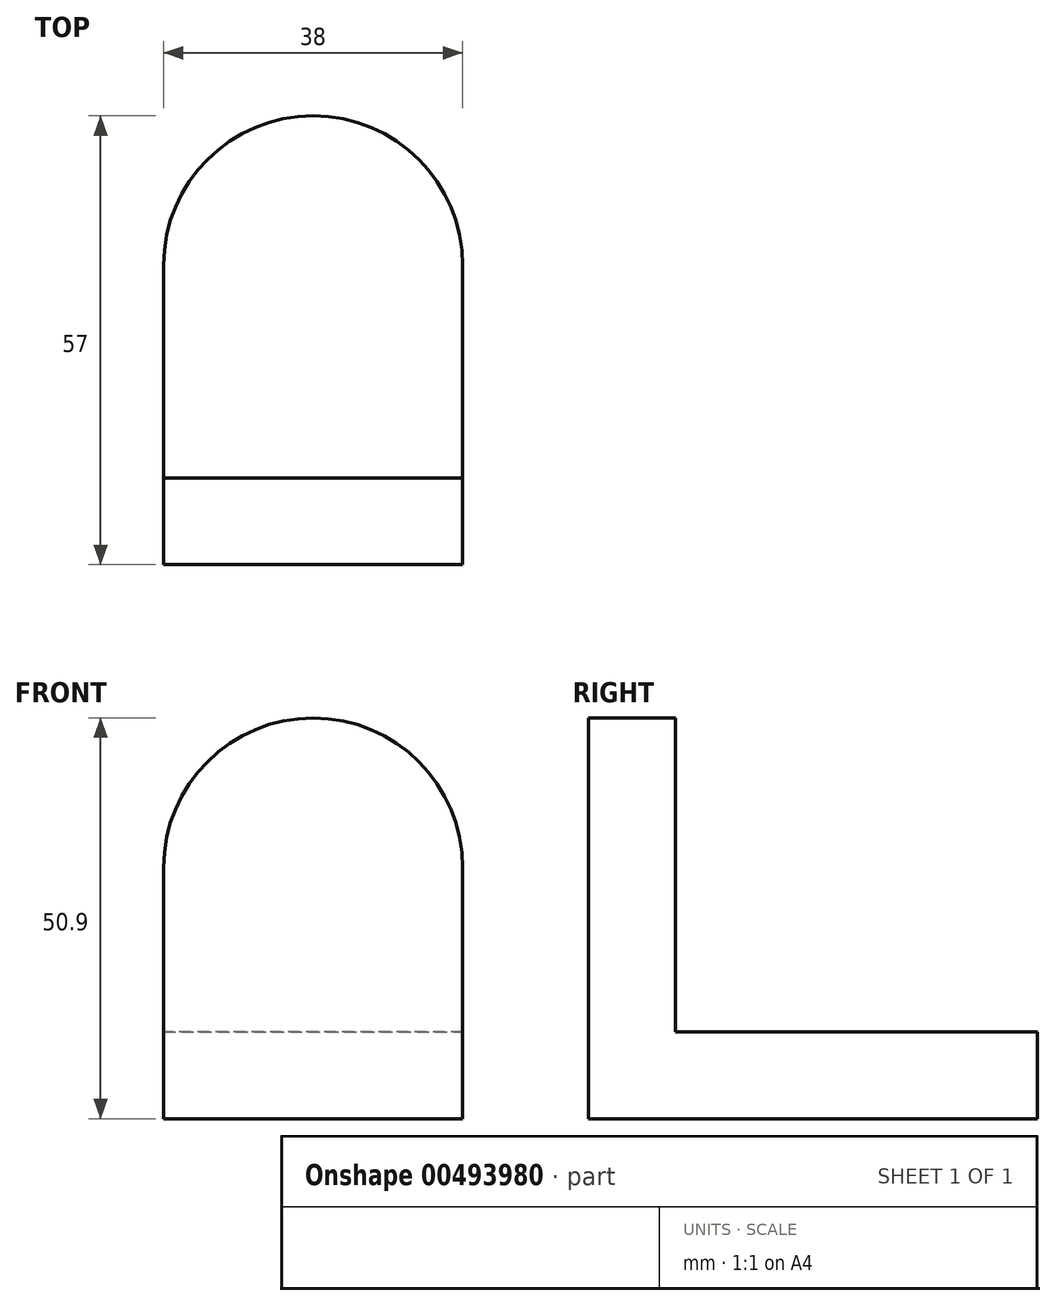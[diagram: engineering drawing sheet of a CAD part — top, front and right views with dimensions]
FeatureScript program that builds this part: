
annotation { "Feature Type Name" : "Feature", "Feature Type Description" : "" }
export const myFeature = defineFeature(function(context is Context, id is Id, definition is map)
    precondition{}
    {
        {
            var Q0;
            Q0=qCreatedBy(makeId("Right.planeOp"),FACE);
            var sketch = newSketch(context, id + "F0", { "sketchPlane" : qUnion([Q0])});
            skLineSegment(sketch, "E0", {"start": v(-17.26, 31.97) * mm, "end": v(-17.26, -18.93) * mm});
            skLineSegment(sketch, "E1", {"start": v(-17.26, -18.93) * mm, "end": v(39.74, -18.93) * mm});
            skLineSegment(sketch, "E2", {"start": v(39.74, -18.93) * mm, "end": v(39.74, -7.93) * mm});
            skLineSegment(sketch, "E3", {"start": v(39.74, -7.93) * mm, "end": v(-6.26, -7.93) * mm});
            skLineSegment(sketch, "E4", {"start": v(-6.26, -7.93) * mm, "end": v(-6.26, 31.97) * mm});
            skLineSegment(sketch, "E5", {"start": v(-6.26, 31.97) * mm, "end": v(-17.26, 31.97) * mm});
            skSolve(sketch);
        }
        {
            var Q0;
            Q0=makeQuery(id+"F0.imprint","IMPRINT",FACE,{"disambiguationData":[TD([[makeQuery(id+"F0.imprint","IMPRINT",EDGE,{"derivedFrom":sQuery(id+"F0.wireOp",EDGE,"E0")}),1.0]])]});
            extrude(context, id + "F1", {"entities" : qUnion([Q0]), "depth" : 38 * mm});
        }
        {
            var Q0;
            Q0=makeQuery(id+"F1.opExtrude","CAP_EDGE",EDGE,{"disambiguationData":[OSD([sQuery(id+"F0.wireOp",EDGE,"E5")])],"isStart":false});
            var Q1;
            Q1=makeQuery(id+"F1.opExtrude","CAP_EDGE",EDGE,{"disambiguationData":[OSD([sQuery(id+"F0.wireOp",EDGE,"E5")])],"isStart":true});
            fillet(context, id + "F2", {"entities" : qUnion([Q0, Q1]), "radius" : 19 * mm, "tangentPropagation" : true, "allowEdgeOverflow" : false});
        }
        {
            var Q0;
            Q0=makeQuery(id+"F1.opExtrude","CAP_EDGE",EDGE,{"disambiguationData":[OSD([sQuery(id+"F0.wireOp",EDGE,"E2")])],"isStart":false});
            var Q1;
            Q1=makeQuery(id+"F1.opExtrude","CAP_EDGE",EDGE,{"disambiguationData":[OSD([sQuery(id+"F0.wireOp",EDGE,"E2")])],"isStart":true});
            fillet(context, id + "F3", {"entities" : qUnion([Q0, Q1]), "radius" : 19 * mm, "tangentPropagation" : true, "allowEdgeOverflow" : false});
        }
    });
